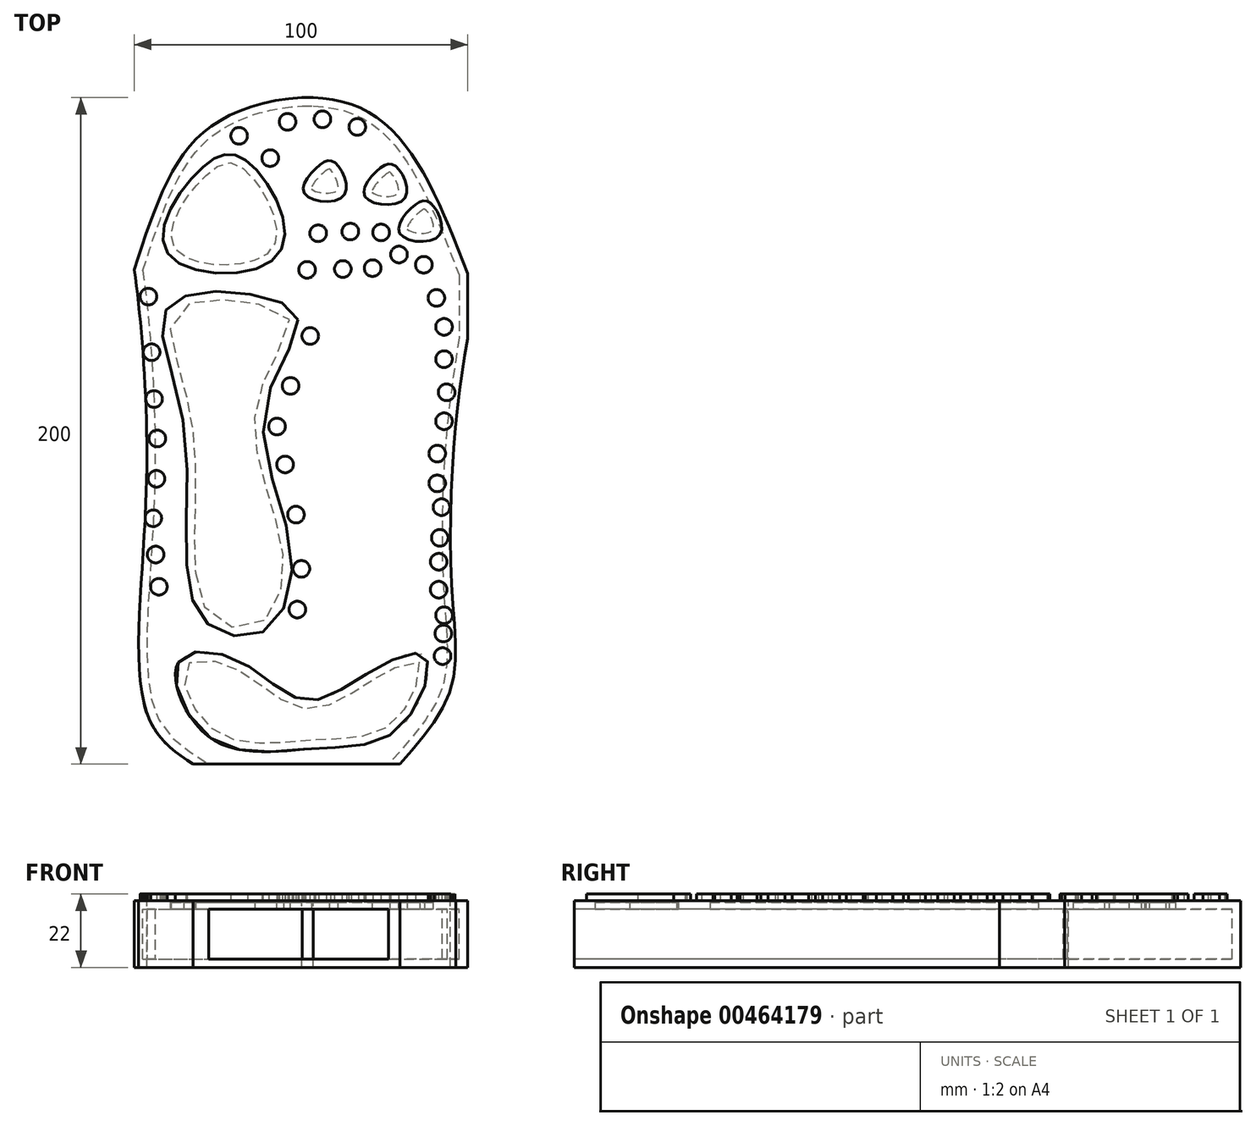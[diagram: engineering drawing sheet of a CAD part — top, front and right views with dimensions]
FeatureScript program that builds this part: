
annotation { "Feature Type Name" : "Feature", "Feature Type Description" : "" }
export const myFeature = defineFeature(function(context is Context, id is Id, definition is map)
    precondition{}
    {
        {
            var Q0;
            Q0=qCreatedBy(makeId("Top.planeOp"),FACE);
            var sketch = newSketch(context, id + "F0", { "sketchPlane" : qUnion([Q0])});
            skLineSegment(sketch, "E0.bottom", {"start": v(-79.68, 75.9) * mm, "end": v(20.32, 75.9) * mm});
            skLineSegment(sketch, "E0.top", {"start": v(-79.68, -124.1) * mm, "end": v(20.32, -124.1) * mm});
            skLineSegment(sketch, "E0.left", {"start": v(-79.68, 75.9) * mm, "end": v(-79.68, -124.1) * mm});
            skLineSegment(sketch, "E0.right", {"start": v(20.32, 75.9) * mm, "end": v(20.32, -124.1) * mm});
            skSolve(sketch);
        }
        {
            var Q0;
            Q0=makeQuery(id+"F0.imprint","IMPRINT",FACE,{"disambiguationData":[TD([[makeQuery(id+"F0.imprint","IMPRINT",EDGE,{"derivedFrom":sQuery(id+"F0.wireOp",EDGE,"E0.bottom")}),-1.0]])]});
            extrude(context, id + "F1", {"entities" : qUnion([Q0]), "depth" : 20 * mm});
        }
        {
            var Q0;
            Q0=makeQuery(id+"F1.opExtrude","CAP_FACE",FACE,{"disambiguationData":[OSD([sQuery(id+"F0.wireOp",EDGE,"E0.bottom"),sQuery(id+"F0.wireOp",EDGE,"E0.top"),sQuery(id+"F0.wireOp",EDGE,"E0.left"),sQuery(id+"F0.wireOp",EDGE,"E0.right")])],"isStart":false});
            var sketch = newSketch(context, id + "F2", { "sketchPlane" : qUnion([Q0])});
            skFitSpline(sketch, "E1", {"points": [v(-79.68, 24.29) * mm, v(-67.37, 55.27) * mm, v(-48.62, 71.72) * mm, v(-9.63, 71.72) * mm, v(20.32, 23.17) * mm], "startDerivative": vector(46.05, 143.22) * mm, "endDerivative": vector(76.52, -198.28) * mm});
            skSolve(sketch);
        }
        {
            var Q0;
            Q0 = qSketchRegion(id + "F2", true);
            var Q1;
            {var subQ0=sQuery(id+"F2.wireOp",EDGE,"6a161702-440d-412a-b4cb-f89826cfb4a0");Q1=makeQuery(id+"F2.imprint","IMPRINT",FACE,{"disambiguationData":[TD([[makeQuery(id+"F2.imprint","IMPRINT",EDGE,{"derivedFrom":subQ0}),1.0]])]});}
            var Q2;
            {var subQ0=sQuery(id+"F2.wireOp",EDGE,"E1");var subQ1=makeQuery(id+"F1.opExtrude","CAP_EDGE",EDGE,{"disambiguationData":[OSD([sQuery(id+"F0.wireOp",EDGE,"E0.right")])],"isStart":false});var subQ2=makeQuery(id+"F2.imprint","INTERSECT",VERTEX,{"derivedFrom":[subQ1,subQ0]});Q2=makeQuery(id+"F2.imprint","IMPRINT",FACE,{"disambiguationData":[TD([[makeQuery(id+"F2.imprint","IMPRINT",EDGE,{"disambiguationData":[TD([[subQ2,1.0]])],"derivedFrom":subQ0}),1.0]])]});}
            var Q3;
            {var subQ0=sQuery(id+"F2.wireOp",EDGE,"E1");var subQ1=makeQuery(id+"F1.opExtrude","CAP_EDGE",EDGE,{"disambiguationData":[OSD([sQuery(id+"F0.wireOp",EDGE,"E0.left")])],"isStart":false});var subQ2=makeQuery(id+"F2.imprint","INTERSECT",VERTEX,{"derivedFrom":[subQ1,subQ0]});Q3=makeQuery(id+"F2.imprint","IMPRINT",FACE,{"disambiguationData":[TD([[makeQuery(id+"F2.imprint","IMPRINT",EDGE,{"disambiguationData":[TD([[subQ2,-1.0]])],"derivedFrom":subQ0}),1.0]])]});}
            extrude(context, id + "F3", {"entities" : qUnion([Q0, Q1, Q2, Q3]), "operationType" : NewBodyOperationType.REMOVE, "endBound" : BoundingType.THROUGH_ALL, "oppositeDirection" : true, "depth" : 25 * mm});
        }
        {
            var Q0;
            Q0=makeQuery(id+"F1.opExtrude","CAP_FACE",FACE,{"disambiguationData":[OSD([sQuery(id+"F0.wireOp",EDGE,"E0.bottom"),sQuery(id+"F0.wireOp",EDGE,"E0.top"),sQuery(id+"F0.wireOp",EDGE,"E0.left"),sQuery(id+"F0.wireOp",EDGE,"E0.right")])],"isStart":false});
            var sketch = newSketch(context, id + "F4", { "sketchPlane" : qUnion([Q0])});
            skFitSpline(sketch, "E2", {"points": [v(-79.68, 24.29) * mm, v(-76.16, -43.8) * mm, v(-75.78, -109.2) * mm, v(-62.01, -124.1) * mm], "startDerivative": vector(16.89, -124.85) * mm, "endDerivative": vector(72.05, -45.45) * mm});
            skSolve(sketch);
        }
        {
            var Q0;
            {var subQ0=sQuery(id+"F4.wireOp",EDGE,"E2");Q0=makeQuery(id+"F4.imprint","IMPRINT",FACE,{"disambiguationData":[TD([[makeQuery(id+"F4.imprint","IMPRINT",EDGE,{"derivedFrom":subQ0}),-1.0]])]});}
            extrude(context, id + "F5", {"entities" : qUnion([Q0]), "operationType" : NewBodyOperationType.REMOVE, "endBound" : BoundingType.THROUGH_ALL, "oppositeDirection" : true, "depth" : 25 * mm});
        }
        {
            var Q0;
            Q0=makeQuery(id+"F1.opExtrude","CAP_FACE",FACE,{"disambiguationData":[OSD([sQuery(id+"F0.wireOp",EDGE,"E0.bottom"),sQuery(id+"F0.wireOp",EDGE,"E0.top"),sQuery(id+"F0.wireOp",EDGE,"E0.left"),sQuery(id+"F0.wireOp",EDGE,"E0.right")])],"isStart":false});
            var sketch = newSketch(context, id + "F6", { "sketchPlane" : qUnion([Q0])});
            skFitSpline(sketch, "E3", {"points": [v(20.32, 3.63) * mm, v(16.4, -26.2) * mm, v(15.64, -71.72) * mm, v(15.26, -101.56) * mm, v(0, -124.1) * mm], "startDerivative": vector(-18.45, -115.69) * mm, "endDerivative": vector(-83.85, -94.56) * mm});
            skSolve(sketch);
        }
        {
            var Q0;
            {var subQ0=sQuery(id+"F6.wireOp",EDGE,"E3");Q0=makeQuery(id+"F6.imprint","IMPRINT",FACE,{"disambiguationData":[TD([[makeQuery(id+"F6.imprint","IMPRINT",EDGE,{"derivedFrom":subQ0}),1.0]])]});}
            extrude(context, id + "F7", {"entities" : qUnion([Q0]), "operationType" : NewBodyOperationType.REMOVE, "endBound" : BoundingType.THROUGH_ALL, "oppositeDirection" : true, "depth" : 25 * mm});
        }
        {
            var Q0;
            Q0=makeQuery(id+"F1.opExtrude","CAP_FACE",FACE,{"disambiguationData":[OSD([sQuery(id+"F0.wireOp",EDGE,"E0.bottom"),sQuery(id+"F0.wireOp",EDGE,"E0.top"),sQuery(id+"F0.wireOp",EDGE,"E0.left"),sQuery(id+"F0.wireOp",EDGE,"E0.right")])],"isStart":false});
            var sketch = newSketch(context, id + "F8", { "sketchPlane" : qUnion([Q0])});
            skFitSpline(sketch, "E4", {"points": [v(-69.7, 29.23) * mm, v(-58.75, 55.43) * mm, v(-45.45, 56.6) * mm, v(-36.46, 28.83) * mm, v(-69.7, 29.23) * mm]});
            skFitSpline(sketch, "E5", {"points": [v(-23.94, 55.82) * mm, v(-28.63, 47.21) * mm, v(-16.9, 46.43) * mm, v(-19.25, 56.2) * mm, v(-23.94, 55.82) * mm]});
            skFitSpline(sketch, "E6", {"points": [v(-5.77, 54.84) * mm, v(-10.46, 46.23) * mm, v(1.27, 45.45) * mm, v(-1.08, 55.23) * mm, v(-5.77, 54.84) * mm]});
            skFitSpline(sketch, "E7", {"points": [v(4.7, 43.78) * mm, v(0, 35.17) * mm, v(11.73, 34.4) * mm, v(9.39, 44.17) * mm, v(4.7, 43.78) * mm]});
            skFitSpline(sketch, "E8", {"points": [v(-30.59, 9.28) * mm, v(-41.93, 16.32) * mm, v(-63.44, 16.71) * mm, v(-71.26, 9.28) * mm, v(-65, -21.62) * mm, v(-63.83, -66.98) * mm, v(-56.4, -83.01) * mm, v(-40.76, -84.19) * mm, v(-32.55, -61.11) * mm, v(-40.76, -18.1) * mm, v(-30.59, 9.28) * mm]});
            skFitSpline(sketch, "E9", {"points": [v(-66.57, -93.57) * mm, v(-48.97, -92.8) * mm, v(-28.24, -104.91) * mm, v(-7.52, -95.53) * mm, v(7.74, -92) * mm, v(0, -113.13) * mm, v(-25.5, -119.38) * mm, v(-56.8, -116.26) * mm, v(-66.57, -93.57) * mm]});
            skSolve(sketch);
        }
        {
            var Q0;
            Q0=makeQuery(id+"F8.imprint","IMPRINT",FACE,{"disambiguationData":[TD([[makeQuery(id+"F8.imprint","IMPRINT",EDGE,{"derivedFrom":sQuery(id+"F8.wireOp",EDGE,"E4")}),-1.0]])]});
            var Q1;
            Q1=makeQuery(id+"F8.imprint","IMPRINT",FACE,{"disambiguationData":[TD([[makeQuery(id+"F8.imprint","IMPRINT",EDGE,{"derivedFrom":sQuery(id+"F8.wireOp",EDGE,"E5")}),1.0]])]});
            var Q2;
            Q2=makeQuery(id+"F8.imprint","IMPRINT",FACE,{"disambiguationData":[TD([[makeQuery(id+"F8.imprint","IMPRINT",EDGE,{"derivedFrom":sQuery(id+"F8.wireOp",EDGE,"E6")}),1.0]])]});
            var Q3;
            Q3=makeQuery(id+"F8.imprint","IMPRINT",FACE,{"disambiguationData":[TD([[makeQuery(id+"F8.imprint","IMPRINT",EDGE,{"derivedFrom":sQuery(id+"F8.wireOp",EDGE,"E7")}),1.0]])]});
            var Q4;
            Q4=makeQuery(id+"F8.imprint","IMPRINT",FACE,{"disambiguationData":[TD([[makeQuery(id+"F8.imprint","IMPRINT",EDGE,{"derivedFrom":sQuery(id+"F8.wireOp",EDGE,"E8")}),1.0]])]});
            var Q5;
            Q5=makeQuery(id+"F8.imprint","IMPRINT",FACE,{"disambiguationData":[TD([[makeQuery(id+"F8.imprint","IMPRINT",EDGE,{"derivedFrom":sQuery(id+"F8.wireOp",EDGE,"E9")}),-1.0]])]});
            extrude(context, id + "F9", {"entities" : qUnion([Q0, Q1, Q2, Q3, Q4, Q5]), "operationType" : NewBodyOperationType.ADD, "depth" : 2 * mm});
        }
        {
            var Q0;
            Q0=makeQuery(id+"F1.opExtrude","CAP_FACE",FACE,{"disambiguationData":[OSD([sQuery(id+"F0.wireOp",EDGE,"E0.bottom"),sQuery(id+"F0.wireOp",EDGE,"E0.top"),sQuery(id+"F0.wireOp",EDGE,"E0.left"),sQuery(id+"F0.wireOp",EDGE,"E0.right")])],"isStart":false});
            var sketch = newSketch(context, id + "F10", { "sketchPlane" : qUnion([Q0])});
            skCircle(sketch, "E10", {"center": v(-48.24, 64.45) * mm, "radius": 2.5 * mm});
            skCircle(sketch, "E11", {"center": v(-33.7, 68.66) * mm, "radius": 2.5 * mm});
            skCircle(sketch, "E12", {"center": v(-23.23, 69.43) * mm, "radius": 2.5 * mm});
            skCircle(sketch, "E13", {"center": v(-12.77, 67.13) * mm, "radius": 2.5 * mm});
            skCircle(sketch, "E14", {"center": v(-24.5, 35.22) * mm, "radius": 2.5 * mm});
            skCircle(sketch, "E15", {"center": v(-14.86, 35.73) * mm, "radius": 2.5 * mm});
            skCircle(sketch, "E16", {"center": v(-5.62, 35.47) * mm, "radius": 2.5 * mm});
            skCircle(sketch, "E17", {"center": v(-27.83, 24.24) * mm, "radius": 2.5 * mm});
            skCircle(sketch, "E18", {"center": v(-17.1, 24.5) * mm, "radius": 2.5 * mm});
            skCircle(sketch, "E19", {"center": v(-8.17, 24.75) * mm, "radius": 2.5 * mm});
            skCircle(sketch, "E20", {"center": v(-0.26, 28.83) * mm, "radius": 2.5 * mm});
            skCircle(sketch, "E21", {"center": v(7.2, 25.77) * mm, "radius": 2.5 * mm});
            skCircle(sketch, "E22", {"center": v(10.98, 15.81) * mm, "radius": 2.5 * mm});
            skCircle(sketch, "E23", {"center": v(13.27, 7.13) * mm, "radius": 2.5 * mm});
            skCircle(sketch, "E24", {"center": v(13.27, -2.57) * mm, "radius": 2.5 * mm});
            skCircle(sketch, "E25", {"center": v(14.04, -12.52) * mm, "radius": 2.5 * mm});
            skCircle(sketch, "E26", {"center": v(13.27, -21.2) * mm, "radius": 2.5 * mm});
            skCircle(sketch, "E27", {"center": v(11.23, -30.9) * mm, "radius": 2.5 * mm});
            skCircle(sketch, "E28", {"center": v(11.23, -39.84) * mm, "radius": 2.5 * mm});
            skCircle(sketch, "E29", {"center": v(12.5, -46.99) * mm, "radius": 2.5 * mm});
            skCircle(sketch, "E30", {"center": v(12, -56.18) * mm, "radius": 2.5 * mm});
            skCircle(sketch, "E31", {"center": v(11.66, -63.35) * mm, "radius": 2.5 * mm});
            skCircle(sketch, "E32", {"center": v(11.66, -71.73) * mm, "radius": 2.5 * mm});
            skCircle(sketch, "E33", {"center": v(13.29, -79.44) * mm, "radius": 2.5 * mm});
            skCircle(sketch, "E34", {"center": v(13.07, -84.9) * mm, "radius": 2.5 * mm});
            skCircle(sketch, "E35", {"center": v(12.83, -91.67) * mm, "radius": 2.5 * mm});
            skCircle(sketch, "E36", {"center": v(-72.32, -70.87) * mm, "radius": 2.5 * mm});
            skCircle(sketch, "E37", {"center": v(-73.3, -61.2) * mm, "radius": 2.5 * mm});
            skCircle(sketch, "E38", {"center": v(-74.02, -50.31) * mm, "radius": 2.5 * mm});
            skCircle(sketch, "E39", {"center": v(-73.05, -38.46) * mm, "radius": 2.5 * mm});
            skCircle(sketch, "E40", {"center": v(-72.8, -26.36) * mm, "radius": 2.5 * mm});
            skCircle(sketch, "E41", {"center": v(-73.77, -14.5) * mm, "radius": 2.5 * mm});
            skCircle(sketch, "E42", {"center": v(-74.5, -0.48) * mm, "radius": 2.5 * mm});
            skCircle(sketch, "E43", {"center": v(-75.47, 16.21) * mm, "radius": 2.5 * mm});
            skCircle(sketch, "E44", {"center": v(-38.9, 57.77) * mm, "radius": 2.5 * mm});
            skCircle(sketch, "E45", {"center": v(-26.9, 4.4) * mm, "radius": 2.5 * mm});
            skCircle(sketch, "E46", {"center": v(-32.8, -10.57) * mm, "radius": 2.5 * mm});
            skCircle(sketch, "E47", {"center": v(-36.87, -22.78) * mm, "radius": 2.5 * mm});
            skCircle(sketch, "E48", {"center": v(-34.43, -34.17) * mm, "radius": 2.5 * mm});
            skCircle(sketch, "E49", {"center": v(-31.18, -49.22) * mm, "radius": 2.5 * mm});
            skCircle(sketch, "E50", {"center": v(-29.55, -65.5) * mm, "radius": 2.5 * mm});
            skCircle(sketch, "E51", {"center": v(-30.77, -77.7) * mm, "radius": 2.5 * mm});
            skSolve(sketch);
        }
        {
            var Q0;
            Q0=makeQuery(id+"F10.imprint","IMPRINT",FACE,{"disambiguationData":[TD([[makeQuery(id+"F10.imprint","IMPRINT",EDGE,{"derivedFrom":sQuery(id+"F10.wireOp",EDGE,"E10")}),1.0]])]});
            var Q1;
            Q1=makeQuery(id+"F10.imprint","IMPRINT",FACE,{"disambiguationData":[TD([[makeQuery(id+"F10.imprint","IMPRINT",EDGE,{"derivedFrom":sQuery(id+"F10.wireOp",EDGE,"E44")}),1.0]])]});
            var Q2;
            Q2=makeQuery(id+"F10.imprint","IMPRINT",FACE,{"disambiguationData":[TD([[makeQuery(id+"F10.imprint","IMPRINT",EDGE,{"derivedFrom":sQuery(id+"F10.wireOp",EDGE,"E11")}),1.0]])]});
            var Q3;
            Q3=makeQuery(id+"F10.imprint","IMPRINT",FACE,{"disambiguationData":[TD([[makeQuery(id+"F10.imprint","IMPRINT",EDGE,{"derivedFrom":sQuery(id+"F10.wireOp",EDGE,"E12")}),1.0]])]});
            var Q4;
            Q4=makeQuery(id+"F10.imprint","IMPRINT",FACE,{"disambiguationData":[TD([[makeQuery(id+"F10.imprint","IMPRINT",EDGE,{"derivedFrom":sQuery(id+"F10.wireOp",EDGE,"E13")}),1.0]])]});
            var Q5;
            Q5=makeQuery(id+"F10.imprint","IMPRINT",FACE,{"disambiguationData":[TD([[makeQuery(id+"F10.imprint","IMPRINT",EDGE,{"derivedFrom":sQuery(id+"F10.wireOp",EDGE,"E14")}),1.0]])]});
            var Q6;
            Q6=makeQuery(id+"F10.imprint","IMPRINT",FACE,{"disambiguationData":[TD([[makeQuery(id+"F10.imprint","IMPRINT",EDGE,{"derivedFrom":sQuery(id+"F10.wireOp",EDGE,"E15")}),1.0]])]});
            var Q7;
            Q7=makeQuery(id+"F10.imprint","IMPRINT",FACE,{"disambiguationData":[TD([[makeQuery(id+"F10.imprint","IMPRINT",EDGE,{"derivedFrom":sQuery(id+"F10.wireOp",EDGE,"E16")}),1.0]])]});
            var Q8;
            Q8=makeQuery(id+"F10.imprint","IMPRINT",FACE,{"disambiguationData":[TD([[makeQuery(id+"F10.imprint","IMPRINT",EDGE,{"derivedFrom":sQuery(id+"F10.wireOp",EDGE,"E19")}),1.0]])]});
            var Q9;
            Q9=makeQuery(id+"F10.imprint","IMPRINT",FACE,{"disambiguationData":[TD([[makeQuery(id+"F10.imprint","IMPRINT",EDGE,{"derivedFrom":sQuery(id+"F10.wireOp",EDGE,"E18")}),1.0]])]});
            var Q10;
            Q10=makeQuery(id+"F10.imprint","IMPRINT",FACE,{"disambiguationData":[TD([[makeQuery(id+"F10.imprint","IMPRINT",EDGE,{"derivedFrom":sQuery(id+"F10.wireOp",EDGE,"E17")}),1.0]])]});
            var Q11;
            Q11=makeQuery(id+"F10.imprint","IMPRINT",FACE,{"disambiguationData":[TD([[makeQuery(id+"F10.imprint","IMPRINT",EDGE,{"derivedFrom":sQuery(id+"F10.wireOp",EDGE,"E20")}),1.0]])]});
            var Q12;
            Q12=makeQuery(id+"F10.imprint","IMPRINT",FACE,{"disambiguationData":[TD([[makeQuery(id+"F10.imprint","IMPRINT",EDGE,{"derivedFrom":sQuery(id+"F10.wireOp",EDGE,"E21")}),1.0]])]});
            var Q13;
            Q13=makeQuery(id+"F10.imprint","IMPRINT",FACE,{"disambiguationData":[TD([[makeQuery(id+"F10.imprint","IMPRINT",EDGE,{"derivedFrom":sQuery(id+"F10.wireOp",EDGE,"E22")}),1.0]])]});
            var Q14;
            Q14=makeQuery(id+"F10.imprint","IMPRINT",FACE,{"disambiguationData":[TD([[makeQuery(id+"F10.imprint","IMPRINT",EDGE,{"derivedFrom":sQuery(id+"F10.wireOp",EDGE,"E23")}),1.0]])]});
            var Q15;
            Q15=makeQuery(id+"F10.imprint","IMPRINT",FACE,{"disambiguationData":[TD([[makeQuery(id+"F10.imprint","IMPRINT",EDGE,{"derivedFrom":sQuery(id+"F10.wireOp",EDGE,"E24")}),1.0]])]});
            var Q16;
            Q16=makeQuery(id+"F10.imprint","IMPRINT",FACE,{"disambiguationData":[TD([[makeQuery(id+"F10.imprint","IMPRINT",EDGE,{"derivedFrom":sQuery(id+"F10.wireOp",EDGE,"E25")}),1.0]])]});
            var Q17;
            Q17=makeQuery(id+"F10.imprint","IMPRINT",FACE,{"disambiguationData":[TD([[makeQuery(id+"F10.imprint","IMPRINT",EDGE,{"derivedFrom":sQuery(id+"F10.wireOp",EDGE,"E26")}),1.0]])]});
            var Q18;
            Q18=makeQuery(id+"F10.imprint","IMPRINT",FACE,{"disambiguationData":[TD([[makeQuery(id+"F10.imprint","IMPRINT",EDGE,{"derivedFrom":sQuery(id+"F10.wireOp",EDGE,"E27")}),1.0]])]});
            var Q19;
            Q19=makeQuery(id+"F10.imprint","IMPRINT",FACE,{"disambiguationData":[TD([[makeQuery(id+"F10.imprint","IMPRINT",EDGE,{"derivedFrom":sQuery(id+"F10.wireOp",EDGE,"E28")}),1.0]])]});
            var Q20;
            Q20=makeQuery(id+"F10.imprint","IMPRINT",FACE,{"disambiguationData":[TD([[makeQuery(id+"F10.imprint","IMPRINT",EDGE,{"derivedFrom":sQuery(id+"F10.wireOp",EDGE,"E29")}),1.0]])]});
            var Q21;
            Q21=makeQuery(id+"F10.imprint","IMPRINT",FACE,{"disambiguationData":[TD([[makeQuery(id+"F10.imprint","IMPRINT",EDGE,{"derivedFrom":sQuery(id+"F10.wireOp",EDGE,"E30")}),1.0]])]});
            var Q22;
            Q22=makeQuery(id+"F10.imprint","IMPRINT",FACE,{"disambiguationData":[TD([[makeQuery(id+"F10.imprint","IMPRINT",EDGE,{"derivedFrom":sQuery(id+"F10.wireOp",EDGE,"E31")}),1.0]])]});
            var Q23;
            Q23=makeQuery(id+"F10.imprint","IMPRINT",FACE,{"disambiguationData":[TD([[makeQuery(id+"F10.imprint","IMPRINT",EDGE,{"derivedFrom":sQuery(id+"F10.wireOp",EDGE,"E32")}),1.0]])]});
            var Q24;
            Q24=makeQuery(id+"F10.imprint","IMPRINT",FACE,{"disambiguationData":[TD([[makeQuery(id+"F10.imprint","IMPRINT",EDGE,{"derivedFrom":sQuery(id+"F10.wireOp",EDGE,"E33")}),1.0]])]});
            var Q25;
            Q25=makeQuery(id+"F10.imprint","IMPRINT",FACE,{"disambiguationData":[TD([[makeQuery(id+"F10.imprint","IMPRINT",EDGE,{"derivedFrom":sQuery(id+"F10.wireOp",EDGE,"E34")}),1.0]])]});
            var Q26;
            Q26=makeQuery(id+"F10.imprint","IMPRINT",FACE,{"disambiguationData":[TD([[makeQuery(id+"F10.imprint","IMPRINT",EDGE,{"derivedFrom":sQuery(id+"F10.wireOp",EDGE,"E35")}),1.0]])]});
            var Q27;
            {var subQ0=sQuery(id+"F10.wireOp",EDGE,"E45");var subQ1=makeQuery(id+"F9.opExtrude","CAP_EDGE",EDGE,{"disambiguationData":[OSD([sQuery(id+"F8.wireOp",EDGE,"E8")])],"isStart":true});var subQ2=makeQuery(id+"F10.imprint","INTERSECT",VERTEX,{"disambiguationData":[OD(0.0)],"derivedFrom":[subQ1,subQ0]});Q27=makeQuery(id+"F10.imprint","IMPRINT",FACE,{"disambiguationData":[TD([[makeQuery(id+"F10.imprint","IMPRINT",EDGE,{"disambiguationData":[TD([[subQ2,-1.0]])],"derivedFrom":subQ0}),1.0]])]});}
            var Q28;
            Q28=makeQuery(id+"F10.imprint","IMPRINT",FACE,{"disambiguationData":[TD([[makeQuery(id+"F10.imprint","IMPRINT",EDGE,{"derivedFrom":sQuery(id+"F10.wireOp",EDGE,"E46")}),1.0]])]});
            var Q29;
            Q29=makeQuery(id+"F10.imprint","IMPRINT",FACE,{"disambiguationData":[TD([[makeQuery(id+"F10.imprint","IMPRINT",EDGE,{"derivedFrom":sQuery(id+"F10.wireOp",EDGE,"E47")}),1.0]])]});
            var Q30;
            Q30=makeQuery(id+"F10.imprint","IMPRINT",FACE,{"disambiguationData":[TD([[makeQuery(id+"F10.imprint","IMPRINT",EDGE,{"derivedFrom":sQuery(id+"F10.wireOp",EDGE,"E48")}),1.0]])]});
            var Q31;
            Q31=makeQuery(id+"F10.imprint","IMPRINT",FACE,{"disambiguationData":[TD([[makeQuery(id+"F10.imprint","IMPRINT",EDGE,{"derivedFrom":sQuery(id+"F10.wireOp",EDGE,"E49")}),1.0]])]});
            var Q32;
            Q32=makeQuery(id+"F10.imprint","IMPRINT",FACE,{"disambiguationData":[TD([[makeQuery(id+"F10.imprint","IMPRINT",EDGE,{"derivedFrom":sQuery(id+"F10.wireOp",EDGE,"E50")}),1.0]])]});
            var Q33;
            Q33=makeQuery(id+"F10.imprint","IMPRINT",FACE,{"disambiguationData":[TD([[makeQuery(id+"F10.imprint","IMPRINT",EDGE,{"derivedFrom":sQuery(id+"F10.wireOp",EDGE,"E51")}),1.0]])]});
            var Q34;
            Q34=makeQuery(id+"F10.imprint","IMPRINT",FACE,{"disambiguationData":[TD([[makeQuery(id+"F10.imprint","IMPRINT",EDGE,{"derivedFrom":sQuery(id+"F10.wireOp",EDGE,"E43")}),1.0]])]});
            var Q35;
            Q35=makeQuery(id+"F10.imprint","IMPRINT",FACE,{"disambiguationData":[TD([[makeQuery(id+"F10.imprint","IMPRINT",EDGE,{"derivedFrom":sQuery(id+"F10.wireOp",EDGE,"E42")}),1.0]])]});
            var Q36;
            Q36=makeQuery(id+"F10.imprint","IMPRINT",FACE,{"disambiguationData":[TD([[makeQuery(id+"F10.imprint","IMPRINT",EDGE,{"derivedFrom":sQuery(id+"F10.wireOp",EDGE,"E41")}),1.0]])]});
            var Q37;
            Q37=makeQuery(id+"F10.imprint","IMPRINT",FACE,{"disambiguationData":[TD([[makeQuery(id+"F10.imprint","IMPRINT",EDGE,{"derivedFrom":sQuery(id+"F10.wireOp",EDGE,"E40")}),1.0]])]});
            var Q38;
            Q38=makeQuery(id+"F10.imprint","IMPRINT",FACE,{"disambiguationData":[TD([[makeQuery(id+"F10.imprint","IMPRINT",EDGE,{"derivedFrom":sQuery(id+"F10.wireOp",EDGE,"E39")}),1.0]])]});
            var Q39;
            {var subQ0=sQuery(id+"F10.wireOp",EDGE,"E38");var subQ1=makeQuery(id+"F5.boolean.opBoolean","COPY",EDGE,{"derivedFrom":makeQuery(id+"F5.opExtrude","CAP_EDGE",EDGE,{"disambiguationData":[OSD([sQuery(id+"F4.wireOp",EDGE,"E2")])],"isStart":true})});var subQ2=makeQuery(id+"F10.imprint","INTERSECT",VERTEX,{"disambiguationData":[OD(0.0)],"derivedFrom":[subQ1,subQ0]});Q39=makeQuery(id+"F10.imprint","IMPRINT",FACE,{"disambiguationData":[TD([[makeQuery(id+"F10.imprint","IMPRINT",EDGE,{"disambiguationData":[TD([[subQ2,1.0]])],"derivedFrom":subQ0}),1.0]])]});}
            var Q40;
            Q40=makeQuery(id+"F10.imprint","IMPRINT",FACE,{"disambiguationData":[TD([[makeQuery(id+"F10.imprint","IMPRINT",EDGE,{"derivedFrom":sQuery(id+"F10.wireOp",EDGE,"E37")}),1.0]])]});
            var Q41;
            Q41=makeQuery(id+"F10.imprint","IMPRINT",FACE,{"disambiguationData":[TD([[makeQuery(id+"F10.imprint","IMPRINT",EDGE,{"derivedFrom":sQuery(id+"F10.wireOp",EDGE,"E36")}),1.0]])]});
            var Q42;
            Q42=makeQuery(id+"F10.imprint","IMPRINT",FACE,{"disambiguationData":[TD([[makeQuery(id+"F10.imprint","IMPRINT",EDGE,{"derivedFrom":sQuery(id+"F10.wireOp",EDGE,"E45")}),1.0]])]});
            extrude(context, id + "F11", {"entities" : qUnion([Q0, Q1, Q2, Q3, Q4, Q5, Q6, Q7, Q8, Q9, Q10, Q11, Q12, Q13, Q14, Q15, Q16, Q17, Q18, Q19, Q20, Q21, Q22, Q23, Q24, Q25, Q26, Q27, Q28, Q29, Q30, Q31, Q32, Q33, Q34, Q35, Q36, Q37, Q38, Q39, Q40, Q41, Q42]), "operationType" : NewBodyOperationType.ADD, "depth" : 2 * mm});
        }
        {
            var Q0;
            Q0=makeQuery(id+"F1.opExtrude","SWEPT_FACE",FACE,{"disambiguationData":[OSD([sQuery(id+"F0.wireOp",EDGE,"E0.top")])]});
            shell(context, id + "F12", {"entities" : qUnion([Q0]), "thickness" : 2.5 * mm});
        }
    });
